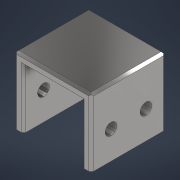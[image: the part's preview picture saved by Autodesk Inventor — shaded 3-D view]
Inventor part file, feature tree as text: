
AUTODESK INVENTOR PART (.ipt)
format: ipt  version: 2021 (Build 250183000, 183)  size: 224,768 bytes
history: native  units: mm
features: sketch x4, extrude x3, chamfer x2, hole x1, fillet x1, other x1
ambient origin geometry x8: Origin, YZ Plane, XZ Plane, XY Plane, X Axis, Y Axis, Z Axis, Center Point
bodies: Solid1 (feature_tree)
feature tree (12):
  extrude  "clamp_base"  Depth=66.0mm
  extrude  "clamp_extrusion"  TaperAngle=0.0deg  [1 undecoded]
  extrude  "platform"  Depth=50.0mm
  hole  "clampHole"  [1 undecoded]
  fillet  "Fillet1"  [1 undecoded]
  chamfer  "Chamfer1"  Distance=1149.0mm
  chamfer  "Chamfer2"  Distance=15.0mm
  other  "weld"
  sketch  "Sketch1"  dims[d0=58.0mm d1=66.0mm]
  sketch  "Sketch2"  dims[d2=33.0mm d3=0.0mm]
  sketch  "Sketch4"  dims[d4=64.0mm d5=0.0mm d6=50.0mm]
  sketch  "Sketch8"  dims[d7=50.0mm d8=25.0mm d9=0.0mm d10=0.0mm d12=1149.0mm d13=15.0mm d14=0.0mm d15=51.0mm d35=0.0mm d36=0.0mm d37=0.0mm d38=0.0mm d51=17.0mm d53=10.0mm d54=6.0mm d55=4.0mm d56=2.0mm d57=90.0deg d58=8.0mm d59=20.594885mm d60=30.0mm d61=64.0mm d81=2.0mm d82=2.0mm d83=2.0mm d84=45.0deg d90=2.0mm d91=2.0mm d92=45.0deg d94=6.981317mm d95=50.0mm d96=10.0mm d97=10.0mm]
note: 3 required parameter values undecoded (feature->parameter linkage not recoverable at this tier; creation-order binding heuristic only, values carry confidence <= 0.55)
